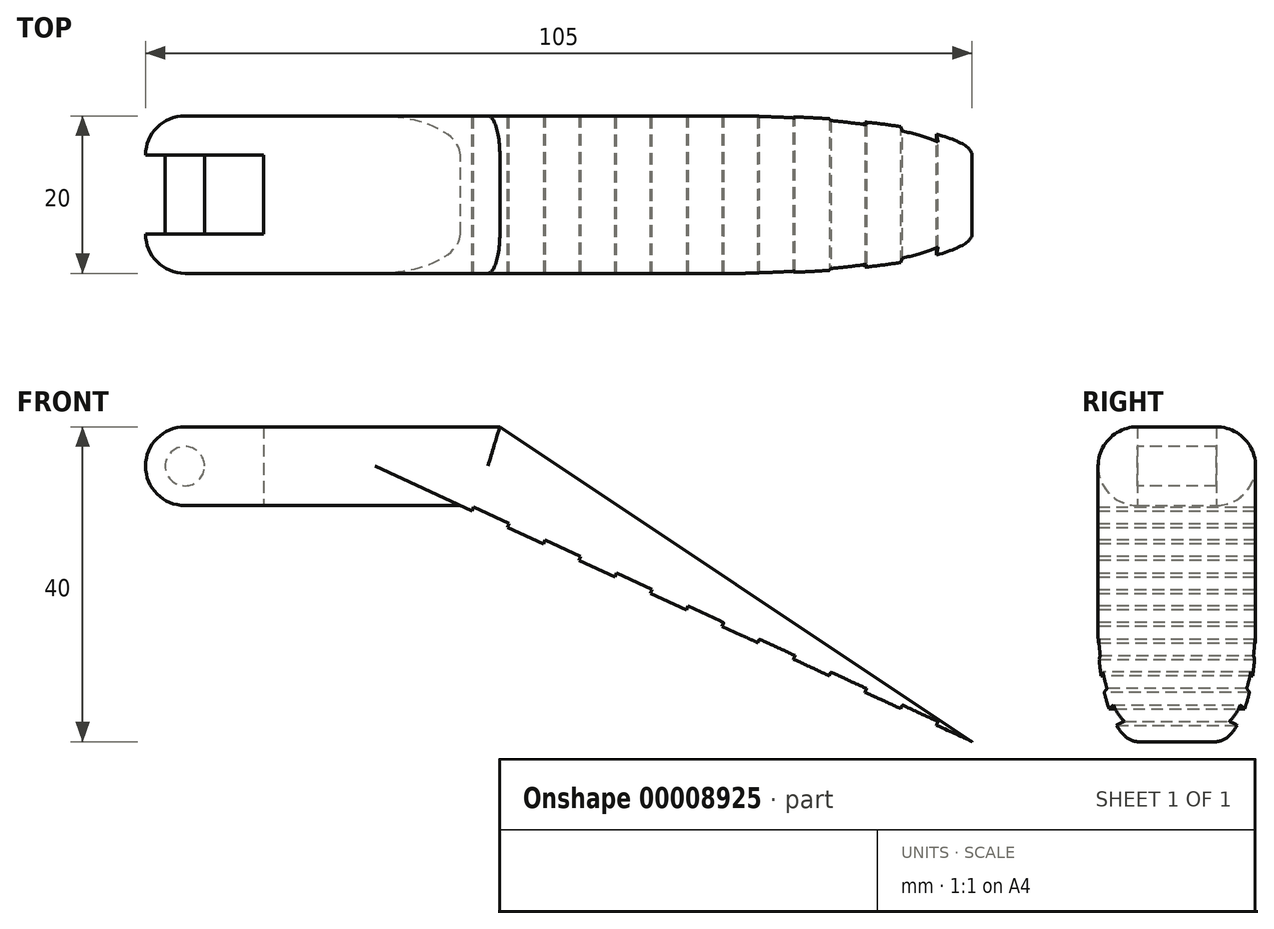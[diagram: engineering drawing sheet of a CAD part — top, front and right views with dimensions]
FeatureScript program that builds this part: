
annotation { "Feature Type Name" : "Feature", "Feature Type Description" : "" }
export const myFeature = defineFeature(function(context is Context, id is Id, definition is map)
    precondition{}
    {
        {
            var Q0;
            Q0=qCreatedBy(makeId("Front.planeOp"),FACE);
            var sketch = newSketch(context, id + "F0", { "sketchPlane" : qUnion([Q0])});
            skLineSegment(sketch, "E0", {"start": v(0, 0) * mm, "end": v(35, 0) * mm});
            skLineSegment(sketch, "E1", {"start": v(35, 0) * mm, "end": v(100, -30) * mm});
            skLineSegment(sketch, "E2", {"start": v(100, -30) * mm, "end": v(40, 10) * mm});
            skLineSegment(sketch, "E3", {"start": v(40, 10) * mm, "end": v(0, 10) * mm});
            skArc(sketch, "E4", {"start": v(0, 10) * mm, "mid": v(-5, 5) * mm, "end": v(0, 0) * mm});
            skSolve(sketch);
        }
        {
            var Q0;
            Q0 = qSketchRegion(id + "F0", true);
            extrude(context, id + "F1", {"entities" : qUnion([Q0]), "depth" : 20 * mm});
        }
        {
            var Q0;
            Q0=makeQuery(id+"F1.opExtrude","SWEPT_FACE",FACE,{"disambiguationData":[OSD([sQuery(id+"F0.wireOp",EDGE,"E0")])]});
            var sketch = newSketch(context, id + "F2", { "sketchPlane" : qUnion([Q0])});
            skLineSegment(sketch, "E5.bottom", {"start": v(10, 5) * mm, "end": v(-16.73, 5) * mm});
            skLineSegment(sketch, "E5.top", {"start": v(10, 15) * mm, "end": v(-16.73, 15) * mm});
            skLineSegment(sketch, "E5.left", {"start": v(10, 5) * mm, "end": v(10, 15) * mm});
            skLineSegment(sketch, "E5.right", {"start": v(-16.73, 5) * mm, "end": v(-16.73, 15) * mm});
            skSolve(sketch);
        }
        {
            var Q0;
            Q0 = qSketchRegion(id + "F2", true);
            extrude(context, id + "F3", {"entities" : qUnion([Q0]), "operationType" : NewBodyOperationType.REMOVE, "oppositeDirection" : true, "depth" : 25 * mm});
        }
        {
            var Q0;
            Q0=makeQuery(id+"F1.opExtrude","CAP_FACE",FACE,{"disambiguationData":[OSD([sQuery(id+"F0.wireOp",EDGE,"E0"),sQuery(id+"F0.wireOp",EDGE,"E1"),sQuery(id+"F0.wireOp",EDGE,"E2"),sQuery(id+"F0.wireOp",EDGE,"E3"),sQuery(id+"F0.wireOp",EDGE,"E4")])],"isStart":false});
            var sketch = newSketch(context, id + "F4", { "sketchPlane" : qUnion([Q0])});
            skCircle(sketch, "E6", {"center": v(0, 5) * mm, "radius": 2.5 * mm});
            skSolve(sketch);
        }
        {
            var Q0;
            Q0 = qSketchRegion(id + "F4", true);
            extrude(context, id + "F5", {"entities" : qUnion([Q0]), "operationType" : NewBodyOperationType.ADD, "oppositeDirection" : true, "depth" : 20 * mm});
        }
        {
            var Q0;
            Q0=makeQuery(id+"F1.opExtrude","SWEPT_FACE",FACE,{"disambiguationData":[OSD([sQuery(id+"F0.wireOp",EDGE,"E1")])]});
            var sketch = newSketch(context, id + "F6", { "sketchPlane" : qUnion([Q0])});
            skLineSegment(sketch, "E7.bottom", {"start": v(98.37, 20) * mm, "end": v(93.37, 20) * mm});
            skLineSegment(sketch, "E7.top", {"start": v(98.37, 0) * mm, "end": v(93.37, 0) * mm});
            skLineSegment(sketch, "E7.left", {"start": v(98.37, 20) * mm, "end": v(98.37, 0) * mm});
            skLineSegment(sketch, "E7.right", {"start": v(93.37, 20) * mm, "end": v(93.37, 0) * mm});
            skLineSegment(sketch, "E8.bottom", {"start": v(88.37, 0) * mm, "end": v(83.37, 0) * mm});
            skLineSegment(sketch, "E8.top", {"start": v(88.37, 20) * mm, "end": v(83.37, 20) * mm});
            skLineSegment(sketch, "E8.left", {"start": v(88.37, 0) * mm, "end": v(88.37, 20) * mm});
            skLineSegment(sketch, "E8.right", {"start": v(83.37, 0) * mm, "end": v(83.37, 20) * mm});
            skLineSegment(sketch, "E9.bottom", {"start": v(78.37, 20) * mm, "end": v(73.37, 20) * mm});
            skLineSegment(sketch, "E9.top", {"start": v(78.37, 0) * mm, "end": v(73.37, 0) * mm});
            skLineSegment(sketch, "E9.left", {"start": v(78.37, 20) * mm, "end": v(78.37, 0) * mm});
            skLineSegment(sketch, "E9.right", {"start": v(73.37, 20) * mm, "end": v(73.37, 0) * mm});
            skLineSegment(sketch, "E10.bottom", {"start": v(68.37, 0) * mm, "end": v(63.37, 0) * mm});
            skLineSegment(sketch, "E10.top", {"start": v(68.37, 20) * mm, "end": v(63.37, 20) * mm});
            skLineSegment(sketch, "E10.left", {"start": v(68.37, 0) * mm, "end": v(68.37, 20) * mm});
            skLineSegment(sketch, "E10.right", {"start": v(63.37, 0) * mm, "end": v(63.37, 20) * mm});
            skLineSegment(sketch, "E11.bottom", {"start": v(58.37, 20) * mm, "end": v(53.37, 20) * mm});
            skLineSegment(sketch, "E11.top", {"start": v(58.37, 0) * mm, "end": v(53.37, 0) * mm});
            skLineSegment(sketch, "E11.left", {"start": v(58.37, 20) * mm, "end": v(58.37, 0) * mm});
            skLineSegment(sketch, "E11.right", {"start": v(53.37, 20) * mm, "end": v(53.37, 0) * mm});
            skLineSegment(sketch, "E12.bottom", {"start": v(48.37, 0) * mm, "end": v(43.37, 0) * mm});
            skLineSegment(sketch, "E12.top", {"start": v(48.37, 20) * mm, "end": v(43.37, 20) * mm});
            skLineSegment(sketch, "E12.left", {"start": v(48.37, 0) * mm, "end": v(48.37, 20) * mm});
            skLineSegment(sketch, "E12.right", {"start": v(43.37, 0) * mm, "end": v(43.37, 20) * mm});
            skLineSegment(sketch, "E13.bottom", {"start": v(38.37, 20) * mm, "end": v(33.37, 20) * mm});
            skLineSegment(sketch, "E13.top", {"start": v(38.37, 0) * mm, "end": v(33.37, 0) * mm});
            skLineSegment(sketch, "E13.left", {"start": v(38.37, 20) * mm, "end": v(38.37, 0) * mm});
            skLineSegment(sketch, "E13.right", {"start": v(33.37, 20) * mm, "end": v(33.37, 0) * mm});
            skSolve(sketch);
        }
        {
            var Q0;
            Q0 = qSketchRegion(id + "F6", true);
            extrude(context, id + "F7", {"entities" : qUnion([Q0]), "operationType" : NewBodyOperationType.REMOVE, "oppositeDirection" : true, "depth" : 0.5 * mm});
        }
        {
            var Q0;
            Q0=makeQuery(id+"F1.opExtrude","CAP_EDGE",EDGE,{"disambiguationData":[OSD([sQuery(id+"F0.wireOp",EDGE,"E2")])],"isStart":true});
            var Q1;
            Q1=makeQuery(id+"F1.opExtrude","CAP_EDGE",EDGE,{"disambiguationData":[OSD([sQuery(id+"F0.wireOp",EDGE,"E3")])],"isStart":true});
            var Q2;
            Q2=makeQuery(id+"F1.opExtrude","CAP_EDGE",EDGE,{"disambiguationData":[OSD([sQuery(id+"F0.wireOp",EDGE,"E3")])],"isStart":false});
            var Q3;
            Q3=makeQuery(id+"F1.opExtrude","CAP_EDGE",EDGE,{"disambiguationData":[OSD([sQuery(id+"F0.wireOp",EDGE,"E2")])],"isStart":false});
            fillet(context, id + "F8", {"entities" : qUnion([Q0, Q1, Q2, Q3]), "radius" : 5 * mm, "tangentPropagation" : true, "allowEdgeOverflow" : false});
        }
    });
